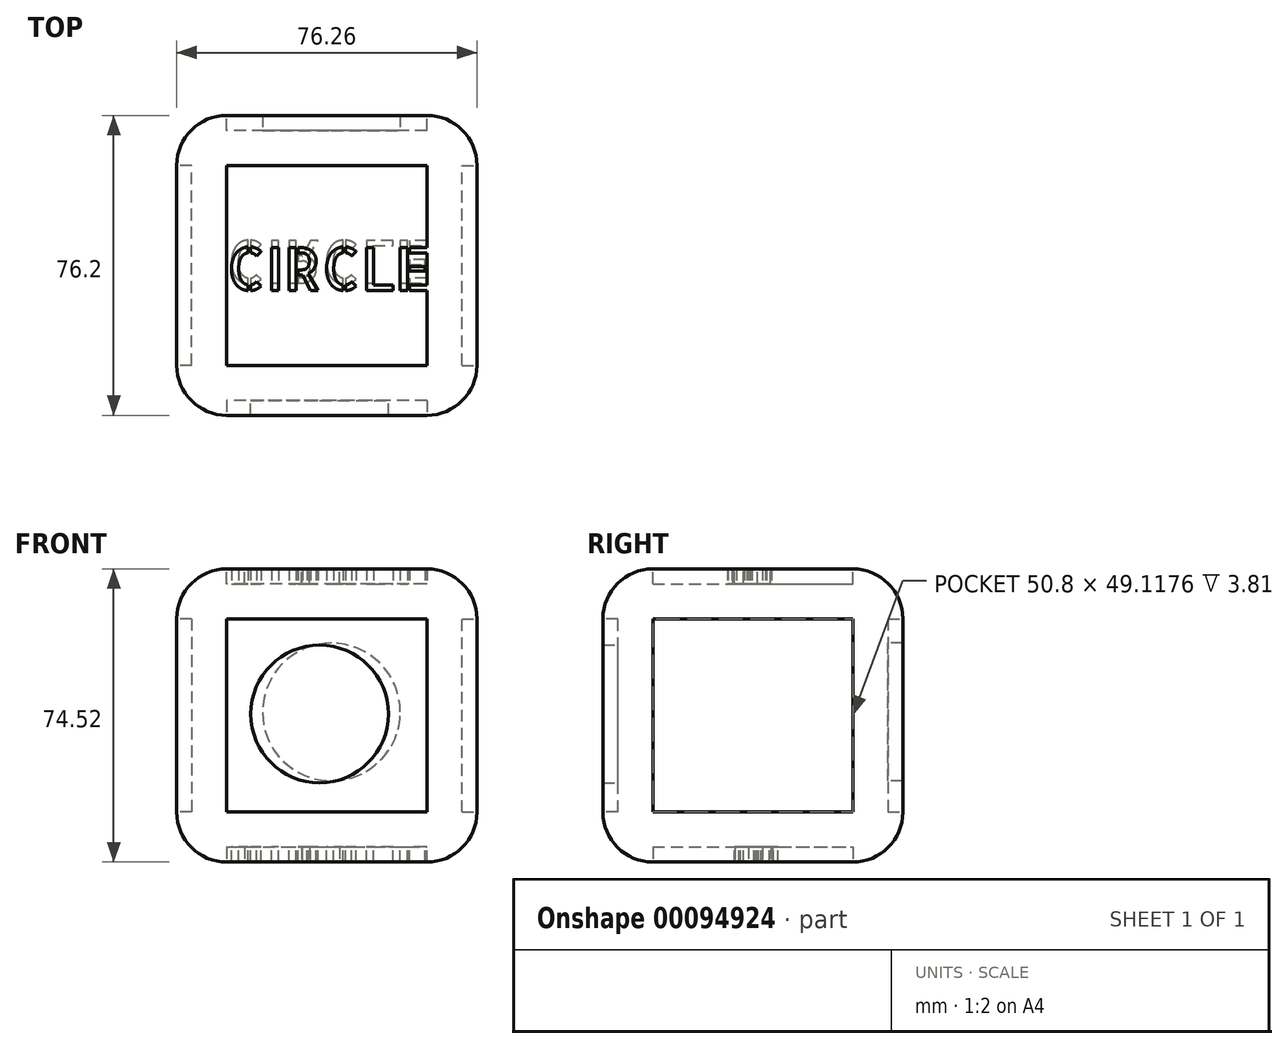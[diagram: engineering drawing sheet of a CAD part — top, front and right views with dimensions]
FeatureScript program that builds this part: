
annotation { "Feature Type Name" : "Feature", "Feature Type Description" : "" }
export const myFeature = defineFeature(function(context is Context, id is Id, definition is map)
    precondition{}
    {
        {
            var Q0;
            Q0=qCreatedBy(makeId("Front.planeOp"),FACE);
            var sketch = newSketch(context, id + "F0", { "sketchPlane" : qUnion([Q0])});
            skLineSegment(sketch, "E0", {"start": v(0, 0) * mm, "end": v(76.26, 0) * mm});
            skLineSegment(sketch, "E1", {"start": v(76.26, 0) * mm, "end": v(76.26, 74.52) * mm});
            skLineSegment(sketch, "E2", {"start": v(76.26, 74.52) * mm, "end": v(0, 74.52) * mm});
            skLineSegment(sketch, "E3", {"start": v(0, 74.52) * mm, "end": v(0, 0) * mm});
            skSolve(sketch);
        }
        {
            var Q0;
            Q0 = qSketchRegion(id + "F0", true);
            extrude(context, id + "F1", {"entities" : qUnion([Q0]), "depth" : 76.2 * mm});
        }
        {
            var Q0;
            Q0=makeQuery(id+"F1.opExtrude","CAP_FACE",FACE,{"disambiguationData":[OSD([sQuery(id+"F0.wireOp",EDGE,"E0"),sQuery(id+"F0.wireOp",EDGE,"E1"),sQuery(id+"F0.wireOp",EDGE,"E2"),sQuery(id+"F0.wireOp",EDGE,"E3")])],"isStart":false});
            var Q1;
            Q1=makeQuery(id+"F1.opExtrude","SWEPT_FACE",FACE,{"disambiguationData":[OSD([sQuery(id+"F0.wireOp",EDGE,"E3")])]});
            var Q2;
            Q2=makeQuery(id+"F1.opExtrude","CAP_FACE",FACE,{"disambiguationData":[OSD([sQuery(id+"F0.wireOp",EDGE,"E0"),sQuery(id+"F0.wireOp",EDGE,"E1"),sQuery(id+"F0.wireOp",EDGE,"E2"),sQuery(id+"F0.wireOp",EDGE,"E3")])],"isStart":true});
            var Q3;
            Q3=makeQuery(id+"F1.opExtrude","SWEPT_FACE",FACE,{"disambiguationData":[OSD([sQuery(id+"F0.wireOp",EDGE,"E1")])]});
            fillet(context, id + "F2", {"entities" : qUnion([Q0, Q1, Q2, Q3]), "radius" : 12.7 * mm, "tangentPropagation" : true, "allowEdgeOverflow" : false});
        }
        {
            var Q0;
            Q0=makeQuery(id+"F1.opExtrude","CAP_FACE",FACE,{"disambiguationData":[OSD([sQuery(id+"F0.wireOp",EDGE,"E0"),sQuery(id+"F0.wireOp",EDGE,"E1"),sQuery(id+"F0.wireOp",EDGE,"E2"),sQuery(id+"F0.wireOp",EDGE,"E3")])],"isStart":false});
            var sketch = newSketch(context, id + "F3", { "sketchPlane" : qUnion([Q0])});
            skLineSegment(sketch, "E4.bottom", {"start": v(12.7, 61.82) * mm, "end": v(63.56, 61.82) * mm});
            skLineSegment(sketch, "E4.top", {"start": v(12.7, 12.7) * mm, "end": v(63.56, 12.7) * mm});
            skLineSegment(sketch, "E4.left", {"start": v(12.7, 61.82) * mm, "end": v(12.7, 12.7) * mm});
            skLineSegment(sketch, "E4.right", {"start": v(63.56, 61.82) * mm, "end": v(63.56, 12.7) * mm});
            skSolve(sketch);
        }
        {
            var Q0;
            Q0 = qSketchRegion(id + "F3", true);
            extrude(context, id + "F4", {"entities" : qUnion([Q0]), "operationType" : NewBodyOperationType.REMOVE, "oppositeDirection" : true, "depth" : 3.8 * mm});
        }
        {
            var Q0;
            Q0=makeQuery(id+"F1.opExtrude","SWEPT_FACE",FACE,{"disambiguationData":[OSD([sQuery(id+"F0.wireOp",EDGE,"E3")])]});
            var sketch = newSketch(context, id + "F5", { "sketchPlane" : qUnion([Q0])});
            skLineSegment(sketch, "E5.bottom", {"start": v(12.7, 61.82) * mm, "end": v(63.5, 61.82) * mm});
            skLineSegment(sketch, "E5.top", {"start": v(12.7, 12.7) * mm, "end": v(63.5, 12.7) * mm});
            skLineSegment(sketch, "E5.left", {"start": v(12.7, 61.82) * mm, "end": v(12.7, 12.7) * mm});
            skLineSegment(sketch, "E5.right", {"start": v(63.5, 61.82) * mm, "end": v(63.5, 12.7) * mm});
            skSolve(sketch);
        }
        {
            var Q0;
            Q0 = qSketchRegion(id + "F5", true);
            extrude(context, id + "F6", {"entities" : qUnion([Q0]), "operationType" : NewBodyOperationType.REMOVE, "oppositeDirection" : true, "depth" : 3.8 * mm});
        }
        {
            var Q0;
            Q0=makeQuery(id+"F1.opExtrude","SWEPT_FACE",FACE,{"disambiguationData":[OSD([sQuery(id+"F0.wireOp",EDGE,"E1")])]});
            var sketch = newSketch(context, id + "F7", { "sketchPlane" : qUnion([Q0])});
            skLineSegment(sketch, "E6.bottom", {"start": v(-12.7, 61.82) * mm, "end": v(-63.5, 61.82) * mm});
            skLineSegment(sketch, "E6.top", {"start": v(-12.7, 12.7) * mm, "end": v(-63.5, 12.7) * mm});
            skLineSegment(sketch, "E6.left", {"start": v(-12.7, 61.82) * mm, "end": v(-12.7, 12.7) * mm});
            skLineSegment(sketch, "E6.right", {"start": v(-63.5, 61.82) * mm, "end": v(-63.5, 12.7) * mm});
            skSolve(sketch);
        }
        {
            var Q0;
            Q0 = qSketchRegion(id + "F7", true);
            extrude(context, id + "F8", {"entities" : qUnion([Q0]), "operationType" : NewBodyOperationType.REMOVE, "oppositeDirection" : true, "depth" : 3.8 * mm});
        }
        {
            var Q0;
            Q0=makeQuery(id+"F1.opExtrude","CAP_FACE",FACE,{"disambiguationData":[OSD([sQuery(id+"F0.wireOp",EDGE,"E0"),sQuery(id+"F0.wireOp",EDGE,"E1"),sQuery(id+"F0.wireOp",EDGE,"E2"),sQuery(id+"F0.wireOp",EDGE,"E3")])],"isStart":true});
            var sketch = newSketch(context, id + "F9", { "sketchPlane" : qUnion([Q0])});
            skLineSegment(sketch, "E7.bottom", {"start": v(-12.7, 61.82) * mm, "end": v(-63.56, 61.82) * mm});
            skLineSegment(sketch, "E7.top", {"start": v(-12.7, 12.7) * mm, "end": v(-63.56, 12.7) * mm});
            skLineSegment(sketch, "E7.left", {"start": v(-12.7, 61.82) * mm, "end": v(-12.7, 12.7) * mm});
            skLineSegment(sketch, "E7.right", {"start": v(-63.56, 61.82) * mm, "end": v(-63.56, 12.7) * mm});
            skSolve(sketch);
        }
        {
            var Q0;
            Q0 = qSketchRegion(id + "F9", true);
            extrude(context, id + "F10", {"entities" : qUnion([Q0]), "operationType" : NewBodyOperationType.REMOVE, "depth" : 3.8 * mm});
        }
        {
            var Q0;
            Q0=makeQuery(id+"F1.opExtrude","CAP_FACE",FACE,{"disambiguationData":[OSD([sQuery(id+"F0.wireOp",EDGE,"E0"),sQuery(id+"F0.wireOp",EDGE,"E1"),sQuery(id+"F0.wireOp",EDGE,"E2"),sQuery(id+"F0.wireOp",EDGE,"E3")])],"isStart":true});
            extrude(context, id + "F11", {"entities" : qUnion([Q0]), "operationType" : NewBodyOperationType.REMOVE, "oppositeDirection" : true, "depth" : 3.8 * mm});
        }
        {
            var Q0;
            Q0=makeQuery(id+"F1.opExtrude","SWEPT_FACE",FACE,{"disambiguationData":[OSD([sQuery(id+"F0.wireOp",EDGE,"E2")])]});
            var sketch = newSketch(context, id + "F12", { "sketchPlane" : qUnion([Q0])});
            skSolve(sketch);
        }
        {
            var Q0;
            {var subQ0=sQuery(id+"F0.wireOp",EDGE,"E2");var subQ1=makeQuery(id+"F1.opExtrude","SWEPT_FACE",FACE,{"disambiguationData":[OSD([subQ0])]});Q0=makeQuery(id+"F12.imprint","IMPRINT",FACE,{"disambiguationData":[TD([[makeQuery(id+"F12.imprint","IMPRINT",EDGE,{"derivedFrom":makeQuery(id+"F2.opFillet","BLEND_EDGE",EDGE,{"blendedFrom":[makeQuery(id+"F1.opExtrude","CAP_EDGE",EDGE,{"disambiguationData":[OSD([subQ0])],"isStart":true}),subQ1],"blendedInto":[subQ1]})}),1.0]])]});}
            extrude(context, id + "F13", {"entities" : qUnion([Q0]), "operationType" : NewBodyOperationType.REMOVE, "oppositeDirection" : true, "depth" : 3.8 * mm});
        }
        {
            var Q0;
            Q0=makeQuery(id+"F1.opExtrude","SWEPT_FACE",FACE,{"disambiguationData":[OSD([sQuery(id+"F0.wireOp",EDGE,"E0")])]});
            extrude(context, id + "F14", {"entities" : qUnion([Q0]), "operationType" : NewBodyOperationType.REMOVE, "oppositeDirection" : true, "depth" : 3.8 * mm});
        }
        {
            var Q0;
            Q0=makeQuery(id+"F4.boolean.opBoolean","COPY",FACE,{"derivedFrom":makeQuery(id+"F4.opExtrude","CAP_FACE",FACE,{"disambiguationData":[OSD([sQuery(id+"F3.wireOp",EDGE,"E4.bottom"),sQuery(id+"F3.wireOp",EDGE,"E4.top"),sQuery(id+"F3.wireOp",EDGE,"E4.left"),sQuery(id+"F3.wireOp",EDGE,"E4.right")])],"isStart":false})});
            var sketch = newSketch(context, id + "F15", { "sketchPlane" : qUnion([Q0])});
            skCircle(sketch, "E8", {"center": v(36.3, 37.64) * mm, "radius": 17.49 * mm});
            skSolve(sketch);
        }
        {
            var Q0;
            Q0=makeQuery(id+"F15.imprint","IMPRINT",FACE,{"disambiguationData":[TD([[makeQuery(id+"F15.imprint","IMPRINT",EDGE,{"derivedFrom":sQuery(id+"F15.wireOp",EDGE,"E8")}),1.0]])]});
            extrude(context, id + "F16", {"entities" : qUnion([Q0]), "operationType" : NewBodyOperationType.ADD, "depth" : 3.8 * mm});
        }
        {
            var Q0;
            Q0=makeQuery(id+"F11.boolean.opBoolean","COPY",FACE,{"derivedFrom":makeQuery(id+"F11.opExtrude","CAP_FACE",FACE,{"disambiguationData":[OSD([sQuery(id+"F0.wireOp",EDGE,"E0"),sQuery(id+"F0.wireOp",EDGE,"E1"),sQuery(id+"F0.wireOp",EDGE,"E2"),sQuery(id+"F0.wireOp",EDGE,"E3")])],"isStart":false})});
            var sketch = newSketch(context, id + "F17", { "sketchPlane" : qUnion([Q0])});
            skCircle(sketch, "E9", {"center": v(-39.28, 38.14) * mm, "radius": 17.49 * mm});
            skSolve(sketch);
        }
        {
            var Q0;
            Q0 = qSketchRegion(id + "F17", true);
            extrude(context, id + "F18", {"entities" : qUnion([Q0]), "operationType" : NewBodyOperationType.ADD, "depth" : 3.8 * mm});
        }
        {
            var Q0;
            Q0=makeQuery(id+"F13.boolean.opBoolean","COPY",FACE,{"derivedFrom":makeQuery(id+"F13.opExtrude","CAP_FACE",FACE,{"disambiguationData":[OSD([sQuery(id+"F0.wireOp",EDGE,"E1"),sQuery(id+"F0.wireOp",EDGE,"E2"),sQuery(id+"F0.wireOp",EDGE,"E3")])],"isStart":false})});
            var sketch = newSketch(context, id + "F19", { "sketchPlane" : qUnion([Q0])});
            skText(sketch, "E10", { "text": "CIRCLE\n", "fontName": "AllertaStencil-Regular.ttf"});
            const initialGuessF19  = {"E10": [0.01276, -0.04445, 1, 0, 0.01086]};
            skSetInitialGuess(sketch, initialGuessF19);
            skSolve(sketch);
        }
        {
            var Q0;
            Q0 = qSketchRegion(id + "F19", true);
            extrude(context, id + "F20", {"entities" : qUnion([Q0]), "operationType" : NewBodyOperationType.ADD, "depth" : 3.8 * mm});
        }
        {
            var Q0;
            Q0=makeQuery(id+"F14.boolean.opBoolean","COPY",FACE,{"derivedFrom":makeQuery(id+"F14.opExtrude","CAP_FACE",FACE,{"disambiguationData":[OSD([sQuery(id+"F0.wireOp",EDGE,"E0")])],"isStart":false})});
            var sketch = newSketch(context, id + "F21", { "sketchPlane" : qUnion([Q0])});
            skText(sketch, "E11", { "text": "CIRCLE", "fontName": "AllertaStencil-Regular.ttf"});
            const initialGuessF21  = {"E11": [0.01276, 0.03175, 1, 0, 0.01086]};
            skSetInitialGuess(sketch, initialGuessF21);
            skSolve(sketch);
        }
        {
            var Q0;
            Q0 = qSketchRegion(id + "F21", true);
            extrude(context, id + "F22", {"entities" : qUnion([Q0]), "operationType" : NewBodyOperationType.ADD, "depth" : 3.8 * mm});
        }
    });
